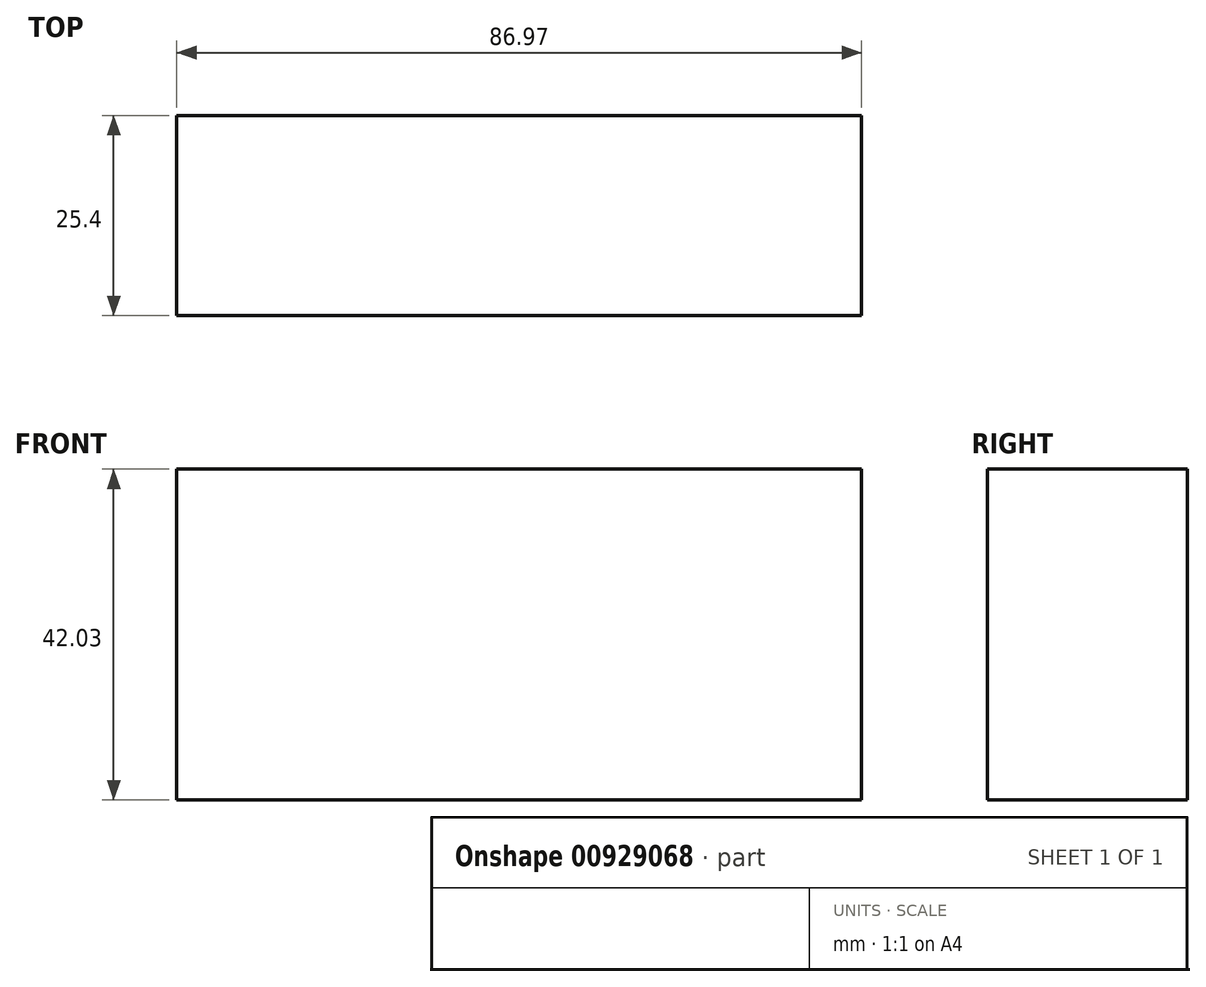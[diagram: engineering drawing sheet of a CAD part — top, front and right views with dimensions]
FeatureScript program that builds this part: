
annotation { "Feature Type Name" : "Feature", "Feature Type Description" : "" }
export const myFeature = defineFeature(function(context is Context, id is Id, definition is map)
    precondition{}
    {
        {
            var Q0;
            Q0=qCreatedBy(makeId("Front.planeOp"),FACE);
            var sketch = newSketch(context, id + "F0", { "sketchPlane" : qUnion([Q0])});
            skLineSegment(sketch, "E0.bottom", {"start": v(-53.4, 21.99) * mm, "end": v(33.58, 21.99) * mm});
            skLineSegment(sketch, "E0.top", {"start": v(-53.4, -20.04) * mm, "end": v(33.58, -20.04) * mm});
            skLineSegment(sketch, "E0.left", {"start": v(-53.4, 21.99) * mm, "end": v(-53.4, -20.04) * mm});
            skLineSegment(sketch, "E0.right", {"start": v(33.58, 21.99) * mm, "end": v(33.58, -20.04) * mm});
            skSolve(sketch);
        }
        {
            var Q0;
            Q0=makeQuery(id+"F0.imprint","IMPRINT",FACE,{"disambiguationData":[TD([[makeQuery(id+"F0.imprint","IMPRINT",EDGE,{"derivedFrom":sQuery(id+"F0.wireOp",EDGE,"E0.bottom")}),-1.0]])]});
            extrude(context, id + "F1", {"entities" : qUnion([Q0]), "oppositeDirection" : true, "depth" : 25.4 * mm, "offsetDistance" : 25.4 * mm});
        }
    });
